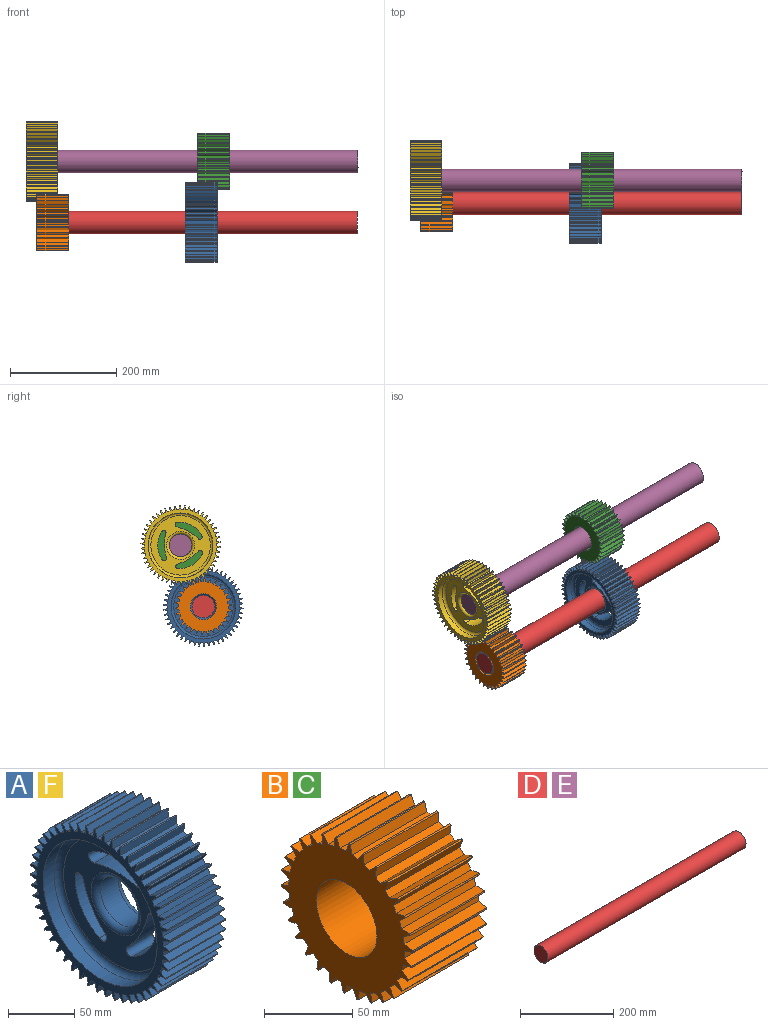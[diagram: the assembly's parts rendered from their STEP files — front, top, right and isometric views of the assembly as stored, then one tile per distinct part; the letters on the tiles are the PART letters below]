
ASSEMBLY  parts=6 mates=5
PART A: 224 faces, bbox 59.5x149x148.9 mm
  f0: cylinder r=81.78mm len=39.56mm, axis (-1,0,0), area 1328.5mm2, adj f1,f3,f12,f220
  f1: cylinder r=4.28mm len=28.36mm, axis (-1,0,0), area 346.5mm2, adj f0,f2,f12,f220
  f2: cylinder r=47.37mm len=44.32mm, axis (-1,0,0), area 1538.2mm2, adj f1,f3,f12,f220
  f3: cylinder r=4.6mm len=28.36mm, axis (-1,0,0), area 409.8mm2, adj f0,f2,f12,f220
  f4: cylinder r=81.78mm len=40.47mm, axis (-1,0,0), area 1328.5mm2, adj f5,f7,f12,f220
  f5: cylinder r=4.28mm len=28.36mm, axis (-1,0,0), area 346.5mm2, adj f4,f6,f12,f220
  f6: cylinder r=47.37mm len=44.58mm, axis (-1,0,0), area 1538.2mm2, adj f5,f7,f12,f220
  f7: cylinder r=4.6mm len=28.36mm, axis (-1,0,0), area 409.8mm2, adj f4,f6,f12,f220
  f8: cylinder r=81.78mm len=46.2mm, axis (-1,0,0), area 1328.5mm2, adj f9,f11,f12,f220
  f9: cylinder r=4.28mm len=28.36mm, axis (-1,0,0), area 346.5mm2, adj f8,f10,f12,f220
  f10: cylinder r=47.37mm len=51.33mm, axis (-1,0,0), area 1538.2mm2, adj f9,f11,f12,f220
  f11: cylinder r=4.6mm len=28.36mm, axis (-1,0,0), area 409.8mm2, adj f8,f10,f12,f220
  f12: plane 111.67x111.67mm, normal (-1,0,0), area 5713.3mm2, adj f0,f1,f2,f3,f4,f5,f6,f7
  f13: cylinder r=74.5mm len=59.54mm, axis (-1,0,0), area 64mm2, adj f62,f66,f212,f216
  f14: cylinder r=74.5mm len=59.54mm, axis (-1,0,0), area 64mm2, adj f62,f209,f213,f216
  f15: cylinder r=74.5mm len=59.54mm, axis (-1,0,0), area 64mm2, adj f62,f206,f210,f216
  f16: cylinder r=74.5mm len=59.54mm, axis (-1,0,0), area 64mm2, adj f62,f203,f207,f216
  f17: cylinder r=74.5mm len=59.54mm, axis (-1,0,0), area 64mm2, adj f62,f200,f204,f216
  f18: cylinder r=74.5mm len=59.54mm, axis (-1,0,0), area 64mm2, adj f62,f197,f201,f216
  f19: cylinder r=74.5mm len=59.54mm, axis (-1,0,0), area 64mm2, adj f62,f194,f198,f216
  f20: cylinder r=74.5mm len=59.54mm, axis (-1,0,0), area 64mm2, adj f62,f191,f195,f216
  f21: cylinder r=74.5mm len=59.54mm, axis (-1,0,0), area 64mm2, adj f62,f188,f192,f216
  f22: cylinder r=74.5mm len=59.54mm, axis (-1,0,0), area 64mm2, adj f62,f185,f189,f216
  f23: cylinder r=74.5mm len=59.54mm, axis (-1,0,0), area 64mm2, adj f62,f182,f186,f216
  f24: cylinder r=74.5mm len=59.54mm, axis (-1,0,0), area 64mm2, adj f62,f179,f183,f216
  f25: cylinder r=74.5mm len=59.54mm, axis (-1,0,0), area 64mm2, adj f62,f176,f180,f216
  f26: cylinder r=74.5mm len=59.54mm, axis (-1,0,0), area 64mm2, adj f62,f173,f177,f216
  f27: cylinder r=74.5mm len=59.54mm, axis (-1,0,0), area 64mm2, adj f62,f170,f174,f216
  f28: cylinder r=74.5mm len=59.54mm, axis (-1,0,0), area 64mm2, adj f62,f167,f171,f216
  f29: cylinder r=74.5mm len=59.54mm, axis (-1,0,0), area 64mm2, adj f62,f164,f168,f216
  f30: cylinder r=74.5mm len=59.54mm, axis (-1,0,0), area 64mm2, adj f62,f161,f165,f216
  f31: cylinder r=74.5mm len=59.54mm, axis (-1,0,0), area 64mm2, adj f62,f158,f162,f216
  f32: cylinder r=74.5mm len=59.54mm, axis (-1,0,0), area 64mm2, adj f62,f155,f159,f216
  f33: cylinder r=74.5mm len=59.54mm, axis (-1,0,0), area 64mm2, adj f62,f152,f156,f216
  f34: cylinder r=74.5mm len=59.54mm, axis (-1,0,0), area 64mm2, adj f62,f149,f153,f216
  f35: cylinder r=74.5mm len=59.54mm, axis (-1,0,0), area 64mm2, adj f62,f146,f150,f216
  f36: cylinder r=74.5mm len=59.54mm, axis (-1,0,0), area 64mm2, adj f62,f143,f147,f216
  f37: cylinder r=74.5mm len=59.54mm, axis (-1,0,0), area 64mm2, adj f62,f140,f144,f216
  f38: cylinder r=74.5mm len=59.54mm, axis (-1,0,0), area 64mm2, adj f62,f137,f141,f216
  f39: cylinder r=74.5mm len=59.54mm, axis (-1,0,0), area 64mm2, adj f62,f134,f138,f216
  f40: cylinder r=74.5mm len=59.54mm, axis (-1,0,0), area 64mm2, adj f62,f131,f135,f216
  f41: cylinder r=74.5mm len=59.54mm, axis (-1,0,0), area 64mm2, adj f62,f128,f132,f216
  f42: cylinder r=74.5mm len=59.54mm, axis (-1,0,0), area 64mm2, adj f62,f125,f129,f216
  f43: cylinder r=74.5mm len=59.54mm, axis (-1,0,0), area 64mm2, adj f62,f122,f126,f216
  f44: cylinder r=74.5mm len=59.54mm, axis (-1,0,0), area 64mm2, adj f62,f119,f123,f216
  f45: cylinder r=74.5mm len=59.54mm, axis (-1,0,0), area 64mm2, adj f62,f116,f120,f216
  f46: cylinder r=74.5mm len=59.54mm, axis (-1,0,0), area 64mm2, adj f62,f113,f117,f216
  f47: cylinder r=74.5mm len=59.54mm, axis (-1,0,0), area 64mm2, adj f62,f110,f114,f216
  f48: cylinder r=74.5mm len=59.54mm, axis (-1,0,0), area 64mm2, adj f62,f107,f111,f216
  f49: cylinder r=74.5mm len=59.54mm, axis (-1,0,0), area 64mm2, adj f62,f104,f108,f216
  f50: cylinder r=74.5mm len=59.54mm, axis (-1,0,0), area 64mm2, adj f62,f101,f105,f216
  f51: cylinder r=74.5mm len=59.54mm, axis (-1,0,0), area 64mm2, adj f62,f98,f102,f216
  f52: cylinder r=74.5mm len=59.54mm, axis (-1,0,0), area 64mm2, adj f62,f95,f99,f216
  f53: cylinder r=74.5mm len=59.54mm, axis (-1,0,0), area 64mm2, adj f62,f92,f96,f216
  f54: cylinder r=74.5mm len=59.54mm, axis (-1,0,0), area 64mm2, adj f62,f89,f93,f216
  f55: cylinder r=74.5mm len=59.54mm, axis (-1,0,0), area 64mm2, adj f62,f86,f90,f216
  f56: cylinder r=74.5mm len=59.54mm, axis (-1,0,0), area 64mm2, adj f62,f83,f87,f216
  f57: cylinder r=74.5mm len=59.54mm, axis (-1,0,0), area 64mm2, adj f62,f80,f84,f216
  f58: cylinder r=74.5mm len=59.54mm, axis (-1,0,0), area 64mm2, adj f62,f77,f81,f216
  f59: cylinder r=74.5mm len=59.54mm, axis (-1,0,0), area 64mm2, adj f62,f74,f78,f216
  f60: cylinder r=74.5mm len=59.54mm, axis (-1,0,0), area 64mm2, adj f62,f71,f75,f216
  f61: cylinder r=74.5mm len=59.54mm, axis (-1,0,0), area 64mm2, adj f62,f68,f72,f216
  f62: plane 149x148.91mm, normal (1,0,0), area 3689.5mm2, adj f13,f14,f15,f16,f17,f18,f19,f20
  f63: cylinder r=74.5mm len=59.54mm, axis (-1,0,0), area 64mm2, adj f62,f65,f69,f216
  f64: cylinder r=21.34mm len=42.68mm, axis (-1,0,0), area 2526.2mm2, adj f217,f223
  f65: plane 59.54x6.41mm, normal (0,-0.94,0.35), area 407.5mm2, adj f62,f63,f67,f216
  f66: plane 59.54x6.57mm, normal (0,0.98,0.22), area 401.1mm2, adj f13,f62,f67,f216
  f67: plane 59.54x4.4mm, normal (0,0,1), area 262.1mm2, adj f62,f65,f66,f216
  f68: plane 59.54x6.06mm, normal (0,-0.88,0.47), area 407.5mm2, adj f61,f62,f70,f216
  f69: plane 59.54x6.71mm, normal (0,1,0.1), area 401.1mm2, adj f62,f63,f70,f216
  f70: plane 59.54x4.37mm, normal (0,0.13,0.99), area 262.1mm2, adj f62,f68,f69,f216
  f71: plane 59.54x5.61mm, normal (0,-0.82,0.57), area 407.5mm2, adj f60,f62,f73,f216
  f72: plane 59.54x6.73mm, normal (0,1,-0.03), area 401.1mm2, adj f61,f62,f73,f216
  f73: plane 59.54x4.26mm, normal (0,0.25,0.97), area 262.1mm2, adj f62,f71,f72,f216
  f74: plane 59.54x5.07mm, normal (0,-0.74,0.67), area 407.5mm2, adj f59,f62,f76,f216
  f75: plane 59.54x6.66mm, normal (0,0.99,-0.16), area 401.1mm2, adj f60,f62,f76,f216
  f76: plane 59.54x4.09mm, normal (0,0.37,0.93), area 262.1mm2, adj f62,f74,f75,f216
  f77: plane 59.54x5.19mm, normal (0,-0.65,0.76), area 407.5mm2, adj f58,f62,f79,f216
  f78: plane 59.54x6.47mm, normal (0,0.96,-0.28), area 401.1mm2, adj f59,f62,f79,f216
  f79: plane 59.54x3.86mm, normal (0,0.48,0.88), area 262.1mm2, adj f62,f77,f78,f216
  f80: plane 59.54x5.71mm, normal (0,-0.55,0.83), area 407.5mm2, adj f57,f62,f82,f216
  f81: plane 59.54x6.19mm, normal (0,0.92,-0.4), area 401.1mm2, adj f58,f62,f82,f216
  f82: plane 59.54x3.56mm, normal (0,0.59,0.81), area 262.1mm2, adj f62,f80,f81,f216
  f83: plane 59.54x6.14mm, normal (0,-0.44,0.9), area 407.5mm2, adj f56,f62,f85,f216
  f84: plane 59.54x5.8mm, normal (0,0.86,-0.51), area 401.1mm2, adj f57,f62,f85,f216
  f85: plane 59.54x3.21mm, normal (0,0.68,0.73), area 262.1mm2, adj f62,f83,f84,f216
  f86: plane 59.54x6.47mm, normal (0,-0.33,0.95), area 407.5mm2, adj f55,f62,f88,f216
  f87: plane 59.54x5.33mm, normal (0,0.79,-0.61), area 401.1mm2, adj f56,f62,f88,f216
  f88: plane 59.54x3.39mm, normal (0,0.77,0.64), area 262.1mm2, adj f62,f86,f87,f216
  f89: plane 59.54x6.7mm, normal (0,-0.21,0.98), area 407.5mm2, adj f54,f62,f91,f216
  f90: plane 59.54x4.77mm, normal (0,0.71,-0.71), area 401.1mm2, adj f55,f62,f91,f216
  f91: plane 59.54x3.72mm, normal (0,0.84,0.54), area 262.1mm2, adj f62,f89,f90,f216
  f92: plane 59.54x6.82mm, normal (0,-0.08,1), area 407.5mm2, adj f53,f62,f94,f216
  f93: plane 59.54x5.32mm, normal (0,0.61,-0.79), area 401.1mm2, adj f54,f62,f94,f216
  f94: plane 59.54x3.98mm, normal (0,0.9,0.43), area 262.1mm2, adj f62,f92,f93,f216
  f95: plane 59.54x6.84mm, normal (0,0.04,1), area 407.5mm2, adj f52,f62,f97,f216
  f96: plane 59.54x5.8mm, normal (0,0.51,-0.86), area 401.1mm2, adj f53,f62,f97,f216
  f97: plane 59.54x4.19mm, normal (0,0.95,0.31), area 262.1mm2, adj f62,f95,f96,f216
  f98: plane 59.54x6.75mm, normal (0,0.17,0.99), area 407.5mm2, adj f51,f62,f100,f216
  f99: plane 59.54x6.18mm, normal (0,0.4,-0.92), area 401.1mm2, adj f52,f62,f100,f216
  f100: plane 59.54x4.32mm, normal (0,0.98,0.19), area 262.1mm2, adj f62,f98,f99,f216
  f101: plane 59.54x6.55mm, normal (0,0.29,0.96), area 407.5mm2, adj f50,f62,f103,f216
  f102: plane 59.54x6.47mm, normal (0,0.28,-0.96), area 401.1mm2, adj f51,f62,f103,f216
  f103: plane 59.54x4.39mm, normal (0,1,0.06), area 262.1mm2, adj f62,f101,f102,f216
  f104: plane 59.54x6.25mm, normal (0,0.41,0.91), area 407.5mm2, adj f49,f62,f106,f216
  f105: plane 59.54x6.65mm, normal (0,0.16,-0.99), area 401.1mm2, adj f50,f62,f106,f216
  f106: plane 59.54x4.39mm, normal (0,1,-0.06), area 262.1mm2, adj f62,f104,f105,f216
  f107: plane 59.54x5.85mm, normal (0,0.52,0.85), area 407.5mm2, adj f48,f62,f109,f216
  f108: plane 59.54x6.73mm, normal (0,0.03,-1), area 401.1mm2, adj f49,f62,f109,f216
  f109: plane 59.54x4.32mm, normal (0,0.98,-0.19), area 262.1mm2, adj f62,f107,f108,f216
  f110: plane 59.54x5.35mm, normal (0,0.62,0.78), area 407.5mm2, adj f47,f62,f112,f216
  f111: plane 59.54x6.71mm, normal (0,-0.09,-1), area 401.1mm2, adj f48,f62,f112,f216
  f112: plane 59.54x4.19mm, normal (0,0.95,-0.31), area 262.1mm2, adj f62,f110,f111,f216
  f113: plane 59.54x4.9mm, normal (0,0.72,0.7), area 407.5mm2, adj f46,f62,f115,f216
  f114: plane 59.54x6.58mm, normal (0,-0.22,-0.98), area 401.1mm2, adj f47,f62,f115,f216
  f115: plane 59.54x3.98mm, normal (0,0.9,-0.43), area 262.1mm2, adj f62,f113,f114,f216
  f116: plane 59.54x5.46mm, normal (0,0.8,0.6), area 407.5mm2, adj f45,f62,f118,f216
  f117: plane 59.54x6.34mm, normal (0,-0.34,-0.94), area 401.1mm2, adj f46,f62,f118,f216
  f118: plane 59.54x3.72mm, normal (0,0.84,-0.54), area 262.1mm2, adj f62,f116,f117,f216
  f119: plane 59.54x5.94mm, normal (0,0.87,0.5), area 407.5mm2, adj f44,f62,f121,f216
  f120: plane 59.54x6.01mm, normal (0,-0.45,-0.89), area 401.1mm2, adj f45,f62,f121,f216
  f121: plane 59.54x3.39mm, normal (0,0.77,-0.64), area 262.1mm2, adj f62,f119,f120,f216
  f122: plane 59.54x6.32mm, normal (0,0.92,0.39), area 407.5mm2, adj f43,f62,f124,f216
  f123: plane 59.54x5.58mm, normal (0,-0.56,-0.83), area 401.1mm2, adj f44,f62,f124,f216
  f124: plane 59.54x3.21mm, normal (0,0.68,-0.73), area 262.1mm2, adj f62,f122,f123,f216
  f125: plane 59.54x6.6mm, normal (0,0.96,0.27), area 407.5mm2, adj f42,f62,f127,f216
  f126: plane 59.54x5.06mm, normal (0,-0.66,-0.75), area 401.1mm2, adj f43,f62,f127,f216
  f127: plane 59.54x3.56mm, normal (0,0.59,-0.81), area 262.1mm2, adj f62,f125,f126,f216
  f128: plane 59.54x6.77mm, normal (0,0.99,0.14), area 407.5mm2, adj f41,f62,f130,f216
  f129: plane 59.54x5.05mm, normal (0,-0.75,-0.66), area 401.1mm2, adj f42,f62,f130,f216
  f130: plane 59.54x3.86mm, normal (0,0.48,-0.88), area 262.1mm2, adj f62,f128,f129,f216
  f131: plane 59.54x6.84mm, normal (0,1,0.02), area 407.5mm2, adj f40,f62,f133,f216
  f132: plane 59.54x5.57mm, normal (0,-0.83,-0.56), area 401.1mm2, adj f41,f62,f133,f216
  f133: plane 59.54x4.09mm, normal (0,0.37,-0.93), area 262.1mm2, adj f62,f131,f132,f216
  f134: plane 59.54x6.81mm, normal (0,0.99,-0.11), area 407.5mm2, adj f39,f62,f136,f216
  f135: plane 59.54x6mm, normal (0,-0.89,-0.45), area 401.1mm2, adj f40,f62,f136,f216
  f136: plane 59.54x4.26mm, normal (0,0.25,-0.97), area 262.1mm2, adj f62,f134,f135,f216
  f137: plane 59.54x6.66mm, normal (0,0.97,-0.23), area 407.5mm2, adj f38,f62,f139,f216
  f138: plane 59.54x6.34mm, normal (0,-0.94,-0.34), area 401.1mm2, adj f39,f62,f139,f216
  f139: plane 59.54x4.37mm, normal (0,0.13,-0.99), area 262.1mm2, adj f62,f137,f138,f216
  f140: plane 59.54x6.41mm, normal (0,0.94,-0.35), area 407.5mm2, adj f37,f62,f142,f216
  f141: plane 59.54x6.57mm, normal (0,-0.98,-0.22), area 401.1mm2, adj f38,f62,f142,f216
  f142: plane 59.54x4.4mm, normal (0,0,-1), area 262.1mm2, adj f62,f140,f141,f216
  f143: plane 59.54x6.06mm, normal (0,0.88,-0.47), area 407.5mm2, adj f36,f62,f145,f216
  f144: plane 59.54x6.71mm, normal (0,-1,-0.1), area 401.1mm2, adj f37,f62,f145,f216
  f145: plane 59.54x4.37mm, normal (0,-0.13,-0.99), area 262.1mm2, adj f62,f143,f144,f216
  f146: plane 59.54x5.61mm, normal (0,0.82,-0.57), area 407.5mm2, adj f35,f62,f148,f216
  f147: plane 59.54x6.73mm, normal (0,-1,0.03), area 401.1mm2, adj f36,f62,f148,f216
  f148: plane 59.54x4.26mm, normal (0,-0.25,-0.97), area 262.1mm2, adj f62,f146,f147,f216
  f149: plane 59.54x5.07mm, normal (0,0.74,-0.67), area 407.5mm2, adj f34,f62,f151,f216
  f150: plane 59.54x6.66mm, normal (0,-0.99,0.16), area 401.1mm2, adj f35,f62,f151,f216
  f151: plane 59.54x4.09mm, normal (0,-0.37,-0.93), area 262.1mm2, adj f62,f149,f150,f216
  f152: plane 59.54x5.19mm, normal (0,0.65,-0.76), area 407.5mm2, adj f33,f62,f154,f216
  f153: plane 59.54x6.47mm, normal (0,-0.96,0.28), area 401.1mm2, adj f34,f62,f154,f216
  f154: plane 59.54x3.86mm, normal (0,-0.48,-0.88), area 262.1mm2, adj f62,f152,f153,f216
  f155: plane 59.54x5.71mm, normal (0,0.55,-0.83), area 407.5mm2, adj f32,f62,f157,f216
  f156: plane 59.54x6.19mm, normal (0,-0.92,0.4), area 401.1mm2, adj f33,f62,f157,f216
  f157: plane 59.54x3.56mm, normal (0,-0.59,-0.81), area 262.1mm2, adj f62,f155,f156,f216
  f158: plane 59.54x6.14mm, normal (0,0.44,-0.9), area 407.5mm2, adj f31,f62,f160,f216
  f159: plane 59.54x5.8mm, normal (0,-0.86,0.51), area 401.1mm2, adj f32,f62,f160,f216
  f160: plane 59.54x3.21mm, normal (0,-0.68,-0.73), area 262.1mm2, adj f62,f158,f159,f216
  f161: plane 59.54x6.47mm, normal (0,0.33,-0.95), area 407.5mm2, adj f30,f62,f163,f216
  f162: plane 59.54x5.33mm, normal (0,-0.79,0.61), area 401.1mm2, adj f31,f62,f163,f216
  f163: plane 59.54x3.39mm, normal (0,-0.77,-0.64), area 262.1mm2, adj f62,f161,f162,f216
  f164: plane 59.54x6.7mm, normal (0,0.21,-0.98), area 407.5mm2, adj f29,f62,f166,f216
  f165: plane 59.54x4.77mm, normal (0,-0.71,0.71), area 401.1mm2, adj f30,f62,f166,f216
  f166: plane 59.54x3.72mm, normal (0,-0.84,-0.54), area 262.1mm2, adj f62,f164,f165,f216
  f167: plane 59.54x6.82mm, normal (0,0.08,-1), area 407.5mm2, adj f28,f62,f169,f216
  f168: plane 59.54x5.32mm, normal (0,-0.61,0.79), area 401.1mm2, adj f29,f62,f169,f216
  f169: plane 59.54x3.98mm, normal (0,-0.9,-0.43), area 262.1mm2, adj f62,f167,f168,f216
  f170: plane 59.54x6.84mm, normal (0,-0.04,-1), area 407.5mm2, adj f27,f62,f172,f216
  f171: plane 59.54x5.8mm, normal (0,-0.51,0.86), area 401.1mm2, adj f28,f62,f172,f216
  f172: plane 59.54x4.19mm, normal (0,-0.95,-0.31), area 262.1mm2, adj f62,f170,f171,f216
  f173: plane 59.54x6.75mm, normal (0,-0.17,-0.99), area 407.5mm2, adj f26,f62,f175,f216
  f174: plane 59.54x6.18mm, normal (0,-0.4,0.92), area 401.1mm2, adj f27,f62,f175,f216
  f175: plane 59.54x4.32mm, normal (0,-0.98,-0.19), area 262.1mm2, adj f62,f173,f174,f216
  f176: plane 59.54x6.55mm, normal (0,-0.29,-0.96), area 407.5mm2, adj f25,f62,f178,f216
  f177: plane 59.54x6.47mm, normal (0,-0.28,0.96), area 401.1mm2, adj f26,f62,f178,f216
  f178: plane 59.54x4.39mm, normal (0,-1,-0.06), area 262.1mm2, adj f62,f176,f177,f216
  f179: plane 59.54x6.25mm, normal (0,-0.41,-0.91), area 407.5mm2, adj f24,f62,f181,f216
  f180: plane 59.54x6.65mm, normal (0,-0.16,0.99), area 401.1mm2, adj f25,f62,f181,f216
  f181: plane 59.54x4.39mm, normal (0,-1,0.06), area 262.1mm2, adj f62,f179,f180,f216
  f182: plane 59.54x5.85mm, normal (0,-0.52,-0.85), area 407.5mm2, adj f23,f62,f184,f216
  f183: plane 59.54x6.73mm, normal (0,-0.03,1), area 401.1mm2, adj f24,f62,f184,f216
  f184: plane 59.54x4.32mm, normal (0,-0.98,0.19), area 262.1mm2, adj f62,f182,f183,f216
  f185: plane 59.54x5.35mm, normal (0,-0.62,-0.78), area 407.5mm2, adj f22,f62,f187,f216
  f186: plane 59.54x6.71mm, normal (0,0.09,1), area 401.1mm2, adj f23,f62,f187,f216
  f187: plane 59.54x4.19mm, normal (0,-0.95,0.31), area 262.1mm2, adj f62,f185,f186,f216
  f188: plane 59.54x4.9mm, normal (0,-0.72,-0.7), area 407.5mm2, adj f21,f62,f190,f216
  f189: plane 59.54x6.58mm, normal (0,0.22,0.98), area 401.1mm2, adj f22,f62,f190,f216
  f190: plane 59.54x3.98mm, normal (0,-0.9,0.43), area 262.1mm2, adj f62,f188,f189,f216
  f191: plane 59.54x5.46mm, normal (0,-0.8,-0.6), area 407.5mm2, adj f20,f62,f193,f216
  f192: plane 59.54x6.34mm, normal (0,0.34,0.94), area 401.1mm2, adj f21,f62,f193,f216
  f193: plane 59.54x3.72mm, normal (0,-0.84,0.54), area 262.1mm2, adj f62,f191,f192,f216
  f194: plane 59.54x5.94mm, normal (0,-0.87,-0.5), area 407.5mm2, adj f19,f62,f196,f216
  f195: plane 59.54x6.01mm, normal (0,0.45,0.89), area 401.1mm2, adj f20,f62,f196,f216
  f196: plane 59.54x3.39mm, normal (0,-0.77,0.64), area 262.1mm2, adj f62,f194,f195,f216
  f197: plane 59.54x6.32mm, normal (0,-0.92,-0.39), area 407.5mm2, adj f18,f62,f199,f216
  f198: plane 59.54x5.58mm, normal (0,0.56,0.83), area 401.1mm2, adj f19,f62,f199,f216
  f199: plane 59.54x3.21mm, normal (0,-0.68,0.73), area 262.1mm2, adj f62,f197,f198,f216
  f200: plane 59.54x6.6mm, normal (0,-0.96,-0.27), area 407.5mm2, adj f17,f62,f202,f216
  f201: plane 59.54x5.06mm, normal (0,0.66,0.75), area 401.1mm2, adj f18,f62,f202,f216
  f202: plane 59.54x3.56mm, normal (0,-0.59,0.81), area 262.1mm2, adj f62,f200,f201,f216
  f203: plane 59.54x6.77mm, normal (0,-0.99,-0.14), area 407.5mm2, adj f16,f62,f205,f216
  f204: plane 59.54x5.05mm, normal (0,0.75,0.66), area 401.1mm2, adj f17,f62,f205,f216
  f205: plane 59.54x3.86mm, normal (0,-0.48,0.88), area 262.1mm2, adj f62,f203,f204,f216
  f206: plane 59.54x6.84mm, normal (0,-1,-0.02), area 407.5mm2, adj f15,f62,f208,f216
  f207: plane 59.54x5.57mm, normal (0,0.83,0.56), area 401.1mm2, adj f16,f62,f208,f216
  f208: plane 59.54x4.09mm, normal (0,-0.37,0.93), area 262.1mm2, adj f62,f206,f207,f216
  f209: plane 59.54x6.81mm, normal (0,-0.99,0.11), area 407.5mm2, adj f14,f62,f211,f216
  f210: plane 59.54x6mm, normal (0,0.89,0.45), area 401.1mm2, adj f15,f62,f211,f216
  f211: plane 59.54x4.26mm, normal (0,-0.25,0.97), area 262.1mm2, adj f62,f209,f210,f216
  f212: plane 59.54x6.66mm, normal (0,-0.97,0.23), area 407.5mm2, adj f13,f62,f214,f216
  f213: plane 59.54x6.34mm, normal (0,0.94,0.34), area 401.1mm2, adj f14,f62,f214,f216
  f214: plane 59.54x4.37mm, normal (0,-0.13,0.99), area 262.1mm2, adj f62,f212,f213,f216
  f215: cylinder r=60.91mm len=121.83mm, axis (1,0,0), area 4438.2mm2, adj f216,f218
  f216: plane 149x148.91mm, normal (-1,0,0), area 3689.5mm2, adj f13,f14,f15,f16,f17,f18,f19,f20
  f217: torus R=26.42mm, axis (1,0,0), area 1162.5mm2, adj f12,f64
  f218: torus R=55.83mm, axis (1,0,0), area 2961.6mm2, adj f12,f215
  f219: cylinder r=60.91mm len=121.83mm, axis (1,0,0), area 3605.8mm2, adj f62,f221
  f220: plane 111.67x111.67mm, normal (1,0,0), area 5947.2mm2, adj f0,f1,f2,f3,f4,f5,f6,f7
  f221: torus R=55.83mm, axis (1,0,0), area 2961.6mm2, adj f219,f220
  f222: cylinder r=24.97mm len=49.94mm, axis (-1,0,0), area 67.7mm2, adj f220,f223
  f223: torus R=26.42mm, axis (1,0,0), area 925.4mm2, adj f64,f222
PART B: 123 faces, bbox 60x105.3x105.4 mm
  f0: cylinder r=52.72mm len=59.98mm, axis (-1,0,0), area 64.1mm2, adj f1,f32,f117,f122
  f1: plane 105.38x105.29mm, normal (-1,0,0), area 5477.2mm2, adj f0,f2,f3,f4,f5,f6,f7,f8
  f2: cylinder r=52.72mm len=59.98mm, axis (-1,0,0), area 64.1mm2, adj f1,f32,f114,f119
  f3: cylinder r=52.72mm len=59.98mm, axis (-1,0,0), area 64.1mm2, adj f1,f32,f111,f116
  f4: cylinder r=52.72mm len=59.98mm, axis (-1,0,0), area 64.1mm2, adj f1,f32,f108,f113
  f5: cylinder r=52.72mm len=59.98mm, axis (-1,0,0), area 64.1mm2, adj f1,f32,f105,f110
  f6: cylinder r=52.72mm len=59.98mm, axis (-1,0,0), area 64.1mm2, adj f1,f32,f102,f107
  f7: cylinder r=52.72mm len=59.98mm, axis (-1,0,0), area 64.1mm2, adj f1,f32,f99,f104
  f8: cylinder r=52.72mm len=59.98mm, axis (-1,0,0), area 64.1mm2, adj f1,f32,f96,f101
  f9: cylinder r=52.72mm len=59.98mm, axis (-1,0,0), area 64.1mm2, adj f1,f32,f93,f98
  f10: cylinder r=52.72mm len=59.98mm, axis (-1,0,0), area 64.1mm2, adj f1,f32,f90,f95
  f11: cylinder r=52.72mm len=59.98mm, axis (-1,0,0), area 64.1mm2, adj f1,f32,f87,f92
  f12: cylinder r=52.72mm len=59.98mm, axis (-1,0,0), area 64.1mm2, adj f1,f32,f84,f89
  f13: cylinder r=52.72mm len=59.98mm, axis (-1,0,0), area 64.1mm2, adj f1,f32,f81,f86
  f14: cylinder r=52.72mm len=59.98mm, axis (-1,0,0), area 64.1mm2, adj f1,f32,f78,f83
  f15: cylinder r=52.72mm len=59.98mm, axis (-1,0,0), area 64.1mm2, adj f1,f32,f75,f80
  f16: cylinder r=52.72mm len=59.98mm, axis (-1,0,0), area 64.1mm2, adj f1,f32,f72,f77
  f17: cylinder r=52.72mm len=59.98mm, axis (-1,0,0), area 64.1mm2, adj f1,f32,f69,f74
  f18: cylinder r=52.72mm len=59.98mm, axis (-1,0,0), area 64.1mm2, adj f1,f32,f66,f71
  f19: cylinder r=52.72mm len=59.98mm, axis (-1,0,0), area 64.1mm2, adj f1,f32,f63,f68
  f20: cylinder r=52.72mm len=59.98mm, axis (-1,0,0), area 64.1mm2, adj f1,f32,f60,f65
  f21: cylinder r=52.72mm len=59.98mm, axis (-1,0,0), area 64.1mm2, adj f1,f32,f57,f62
  f22: cylinder r=52.72mm len=59.98mm, axis (-1,0,0), area 64.1mm2, adj f1,f32,f54,f59
  f23: cylinder r=52.72mm len=59.98mm, axis (-1,0,0), area 64.1mm2, adj f1,f32,f51,f56
  f24: cylinder r=52.72mm len=59.98mm, axis (-1,0,0), area 64.1mm2, adj f1,f32,f48,f53
  f25: cylinder r=52.72mm len=59.98mm, axis (-1,0,0), area 64.1mm2, adj f1,f32,f45,f50
  f26: cylinder r=52.72mm len=59.98mm, axis (-1,0,0), area 64.1mm2, adj f1,f32,f42,f47
  f27: cylinder r=52.72mm len=59.98mm, axis (-1,0,0), area 64.1mm2, adj f1,f32,f39,f44
  f28: cylinder r=52.72mm len=59.98mm, axis (-1,0,0), area 64.1mm2, adj f1,f32,f36,f41
  f29: cylinder r=52.72mm len=59.98mm, axis (-1,0,0), area 64.1mm2, adj f1,f32,f33,f38
  f30: cylinder r=52.72mm len=59.98mm, axis (-1,0,0), area 64.1mm2, adj f1,f32,f35,f120
  f31: cylinder r=24.38mm len=59.98mm, axis (-1,0,0), area 9188.7mm2, adj f1,f32
  f32: plane 105.38x105.29mm, normal (1,0,0), area 5477.2mm2, adj f0,f2,f3,f4,f5,f6,f7,f8
  f33: plane 59.98x5.71mm, normal (0,-0.89,0.46), area 384.9mm2, adj f1,f29,f32,f34
  f34: plane 59.98x4.84mm, normal (0,0,1), area 290.2mm2, adj f1,f32,f33,f35
  f35: plane 59.98x6.34mm, normal (0,0.95,0.32), area 401.9mm2, adj f1,f30,f32,f34
  f36: plane 59.98x4.98mm, normal (0,-0.78,0.63), area 384.9mm2, adj f1,f28,f32,f37
  f37: plane 59.98x4.73mm, normal (0,0.21,0.98), area 290.2mm2, adj f1,f32,f36,f38
  f38: plane 59.98x6.65mm, normal (0,0.99,0.12), area 401.9mm2, adj f1,f29,f32,f37
  f39: plane 59.98x5mm, normal (0,-0.63,0.78), area 384.9mm2, adj f1,f27,f32,f40
  f40: plane 59.98x4.42mm, normal (0,0.41,0.91), area 290.2mm2, adj f1,f32,f39,f41
  f41: plane 59.98x6.67mm, normal (0,1,-0.09), area 401.9mm2, adj f1,f28,f32,f40
  f42: plane 59.98x5.72mm, normal (0,-0.45,0.89), area 384.9mm2, adj f1,f26,f32,f43
  f43: plane 59.98x3.92mm, normal (0,0.59,0.81), area 290.2mm2, adj f1,f32,f42,f44
  f44: plane 59.98x6.41mm, normal (0,0.96,-0.29), area 401.9mm2, adj f1,f27,f32,f43
  f45: plane 59.98x6.2mm, normal (0,-0.26,0.97), area 384.9mm2, adj f1,f25,f32,f46
  f46: plane 59.98x3.6mm, normal (0,0.74,0.67), area 290.2mm2, adj f1,f32,f45,f47
  f47: plane 59.98x5.86mm, normal (0,0.87,-0.49), area 401.9mm2, adj f1,f26,f32,f46
  f48: plane 59.98x6.41mm, normal (0,-0.05,1), area 384.9mm2, adj f1,f24,f32,f49
  f49: plane 59.98x4.19mm, normal (0,0.87,0.5), area 290.2mm2, adj f1,f32,f48,f50
  f50: plane 59.98x5.05mm, normal (0,0.75,-0.66), area 401.9mm2, adj f1,f25,f32,f49
  f51: plane 59.98x6.34mm, normal (0,0.16,0.99), area 384.9mm2, adj f1,f23,f32,f52
  f52: plane 59.98x4.6mm, normal (0,0.95,0.31), area 290.2mm2, adj f1,f32,f51,f53
  f53: plane 59.98x5.36mm, normal (0,0.6,-0.8), area 401.9mm2, adj f1,f24,f32,f52
  f54: plane 59.98x5.99mm, normal (0,0.36,0.93), area 384.9mm2, adj f1,f22,f32,f55
  f55: plane 59.98x4.81mm, normal (0,0.99,0.1), area 290.2mm2, adj f1,f32,f54,f56
  f56: plane 59.98x6.08mm, normal (0,0.42,-0.91), area 401.9mm2, adj f1,f23,f32,f55
  f57: plane 59.98x5.38mm, normal (0,0.55,0.84), area 384.9mm2, adj f1,f21,f32,f58
  f58: plane 59.98x4.81mm, normal (0,0.99,-0.1), area 290.2mm2, adj f1,f32,f57,f59
  f59: plane 59.98x6.53mm, normal (0,0.22,-0.97), area 401.9mm2, adj f1,f22,f32,f58
  f60: plane 59.98x4.55mm, normal (0,0.71,0.71), area 384.9mm2, adj f1,f20,f32,f61
  f61: plane 59.98x4.6mm, normal (0,0.95,-0.31), area 290.2mm2, adj f1,f32,f60,f62
  f62: plane 59.98x6.7mm, normal (0,0.02,-1), area 401.9mm2, adj f1,f21,f32,f61
  f63: plane 59.98x5.39mm, normal (0,0.84,0.54), area 384.9mm2, adj f1,f19,f32,f64
  f64: plane 59.98x4.19mm, normal (0,0.87,-0.5), area 290.2mm2, adj f1,f32,f63,f65
  f65: plane 59.98x6.58mm, normal (0,-0.19,-0.98), area 401.9mm2, adj f1,f20,f32,f64
  f66: plane 59.98x6mm, normal (0,0.93,0.36), area 384.9mm2, adj f1,f18,f32,f67
  f67: plane 59.98x3.6mm, normal (0,0.74,-0.67), area 290.2mm2, adj f1,f32,f66,f68
  f68: plane 59.98x6.16mm, normal (0,-0.39,-0.92), area 401.9mm2, adj f1,f19,f32,f67
  f69: plane 59.98x6.34mm, normal (0,0.99,0.15), area 384.9mm2, adj f1,f17,f32,f70
  f70: plane 59.98x3.92mm, normal (0,0.59,-0.81), area 290.2mm2, adj f1,f32,f69,f71
  f71: plane 59.98x5.48mm, normal (0,-0.57,-0.82), area 401.9mm2, adj f1,f18,f32,f70
  f72: plane 59.98x6.41mm, normal (0,1,-0.05), area 384.9mm2, adj f1,f16,f32,f73
  f73: plane 59.98x4.42mm, normal (0,0.41,-0.91), area 290.2mm2, adj f1,f32,f72,f74
  f74: plane 59.98x4.91mm, normal (0,-0.73,-0.68), area 401.9mm2, adj f1,f17,f32,f73
  f75: plane 59.98x6.2mm, normal (0,0.97,-0.26), area 384.9mm2, adj f1,f15,f32,f76
  f76: plane 59.98x4.73mm, normal (0,0.21,-0.98), area 290.2mm2, adj f1,f32,f75,f77
  f77: plane 59.98x5.75mm, normal (0,-0.86,-0.51), area 401.9mm2, adj f1,f16,f32,f76
  f78: plane 59.98x5.71mm, normal (0,0.89,-0.46), area 384.9mm2, adj f1,f14,f32,f79
  f79: plane 59.98x4.84mm, normal (0,0,-1), area 290.2mm2, adj f1,f32,f78,f80
  f80: plane 59.98x6.34mm, normal (0,-0.95,-0.32), area 401.9mm2, adj f1,f15,f32,f79
  f81: plane 59.98x4.98mm, normal (0,0.78,-0.63), area 384.9mm2, adj f1,f13,f32,f82
  f82: plane 59.98x4.73mm, normal (0,-0.21,-0.98), area 290.2mm2, adj f1,f32,f81,f83
  f83: plane 59.98x6.65mm, normal (0,-0.99,-0.12), area 401.9mm2, adj f1,f14,f32,f82
  f84: plane 59.98x5mm, normal (0,0.63,-0.78), area 384.9mm2, adj f1,f12,f32,f85
  f85: plane 59.98x4.42mm, normal (0,-0.41,-0.91), area 290.2mm2, adj f1,f32,f84,f86
  f86: plane 59.98x6.67mm, normal (0,-1,0.09), area 401.9mm2, adj f1,f13,f32,f85
  f87: plane 59.98x5.72mm, normal (0,0.45,-0.89), area 384.9mm2, adj f1,f11,f32,f88
  f88: plane 59.98x3.92mm, normal (0,-0.59,-0.81), area 290.2mm2, adj f1,f32,f87,f89
  f89: plane 59.98x6.41mm, normal (0,-0.96,0.29), area 401.9mm2, adj f1,f12,f32,f88
  f90: plane 59.98x6.2mm, normal (0,0.26,-0.97), area 384.9mm2, adj f1,f10,f32,f91
  f91: plane 59.98x3.6mm, normal (0,-0.74,-0.67), area 290.2mm2, adj f1,f32,f90,f92
  f92: plane 59.98x5.86mm, normal (0,-0.87,0.49), area 401.9mm2, adj f1,f11,f32,f91
  f93: plane 59.98x6.41mm, normal (0,0.05,-1), area 384.9mm2, adj f1,f9,f32,f94
  f94: plane 59.98x4.19mm, normal (0,-0.87,-0.5), area 290.2mm2, adj f1,f32,f93,f95
  f95: plane 59.98x5.05mm, normal (0,-0.75,0.66), area 401.9mm2, adj f1,f10,f32,f94
  f96: plane 59.98x6.34mm, normal (0,-0.16,-0.99), area 384.9mm2, adj f1,f8,f32,f97
  f97: plane 59.98x4.6mm, normal (0,-0.95,-0.31), area 290.2mm2, adj f1,f32,f96,f98
  f98: plane 59.98x5.36mm, normal (0,-0.6,0.8), area 401.9mm2, adj f1,f9,f32,f97
  f99: plane 59.98x5.99mm, normal (0,-0.36,-0.93), area 384.9mm2, adj f1,f7,f32,f100
  f100: plane 59.98x4.81mm, normal (0,-0.99,-0.1), area 290.2mm2, adj f1,f32,f99,f101
  f101: plane 59.98x6.08mm, normal (0,-0.42,0.91), area 401.9mm2, adj f1,f8,f32,f100
  f102: plane 59.98x5.38mm, normal (0,-0.55,-0.84), area 384.9mm2, adj f1,f6,f32,f103
  f103: plane 59.98x4.81mm, normal (0,-0.99,0.1), area 290.2mm2, adj f1,f32,f102,f104
  f104: plane 59.98x6.53mm, normal (0,-0.22,0.97), area 401.9mm2, adj f1,f7,f32,f103
  f105: plane 59.98x4.55mm, normal (0,-0.71,-0.71), area 384.9mm2, adj f1,f5,f32,f106
  f106: plane 59.98x4.6mm, normal (0,-0.95,0.31), area 290.2mm2, adj f1,f32,f105,f107
  f107: plane 59.98x6.7mm, normal (0,-0.02,1), area 401.9mm2, adj f1,f6,f32,f106
  f108: plane 59.98x5.39mm, normal (0,-0.84,-0.54), area 384.9mm2, adj f1,f4,f32,f109
  f109: plane 59.98x4.19mm, normal (0,-0.87,0.5), area 290.2mm2, adj f1,f32,f108,f110
  f110: plane 59.98x6.58mm, normal (0,0.19,0.98), area 401.9mm2, adj f1,f5,f32,f109
  f111: plane 59.98x6mm, normal (0,-0.93,-0.36), area 384.9mm2, adj f1,f3,f32,f112
  f112: plane 59.98x3.6mm, normal (0,-0.74,0.67), area 290.2mm2, adj f1,f32,f111,f113
  f113: plane 59.98x6.16mm, normal (0,0.39,0.92), area 401.9mm2, adj f1,f4,f32,f112
  f114: plane 59.98x6.34mm, normal (0,-0.99,-0.15), area 384.9mm2, adj f1,f2,f32,f115
  f115: plane 59.98x3.92mm, normal (0,-0.59,0.81), area 290.2mm2, adj f1,f32,f114,f116
  f116: plane 59.98x5.48mm, normal (0,0.57,0.82), area 401.9mm2, adj f1,f3,f32,f115
  f117: plane 59.98x6.41mm, normal (0,-1,0.05), area 384.9mm2, adj f0,f1,f32,f118
  f118: plane 59.98x4.42mm, normal (0,-0.41,0.91), area 290.2mm2, adj f1,f32,f117,f119
  f119: plane 59.98x4.91mm, normal (0,0.73,0.68), area 401.9mm2, adj f1,f2,f32,f118
  f120: plane 59.98x6.2mm, normal (0,-0.97,0.26), area 384.9mm2, adj f1,f30,f32,f121
  f121: plane 59.98x4.73mm, normal (0,-0.21,0.98), area 290.2mm2, adj f1,f32,f120,f122
  f122: plane 59.98x5.75mm, normal (0,0.86,0.51), area 401.9mm2, adj f0,f1,f32,f121
PART C: same geometry as B
PART D: 3 faces, bbox 602x42.5x42.5 mm
  f0: cylinder r=21.27mm len=601.98mm, axis (-1,0,0), area 80453.8mm2, adj f1,f2
  f1: plane 42.54x42.54mm, normal (1,0,0), area 1421.4mm2, adj f0
  f2: plane 42.54x42.54mm, normal (-1,0,0), area 1421.4mm2, adj f0
PART E: same geometry as D
PART F: same geometry as A
PLACE A rot(axis=(-1,0,0),90deg) t=(-2.49,159.14,-158.41)mm
PLACE B t=(-281.71,547.23,-134.03)mm
PLACE C t=(20.86,590.2,-18.86)mm
PLACE D t=(-324.19,113.4,-112.76)mm
PLACE E t=(-322.61,156.37,2.41)mm
PLACE F rot(axis=(-1,0,0),90deg) t=(-301.9,202.11,-43.24)mm
MATE cylindrical E.f0 <-> C.f0  axis (-1,0,0) through (-21.62,156.37,-43.24)mm
MATE revolute A.f13 <-> D.f0  axis (1,0,0) through (-23.2,113.4,-158.41)mm
MATE revolute F.f13 <-> E.f0  axis (-1,0,0) through (-322.61,156.37,-43.24)mm
MATE revolute B.f0 <-> D.f0  axis (-1,0,0) through (-324.19,113.4,-158.41)mm
MATE revolute C.f0 <-> E.f0  axis (-1,0,0) through (-21.62,156.37,-43.24)mm
